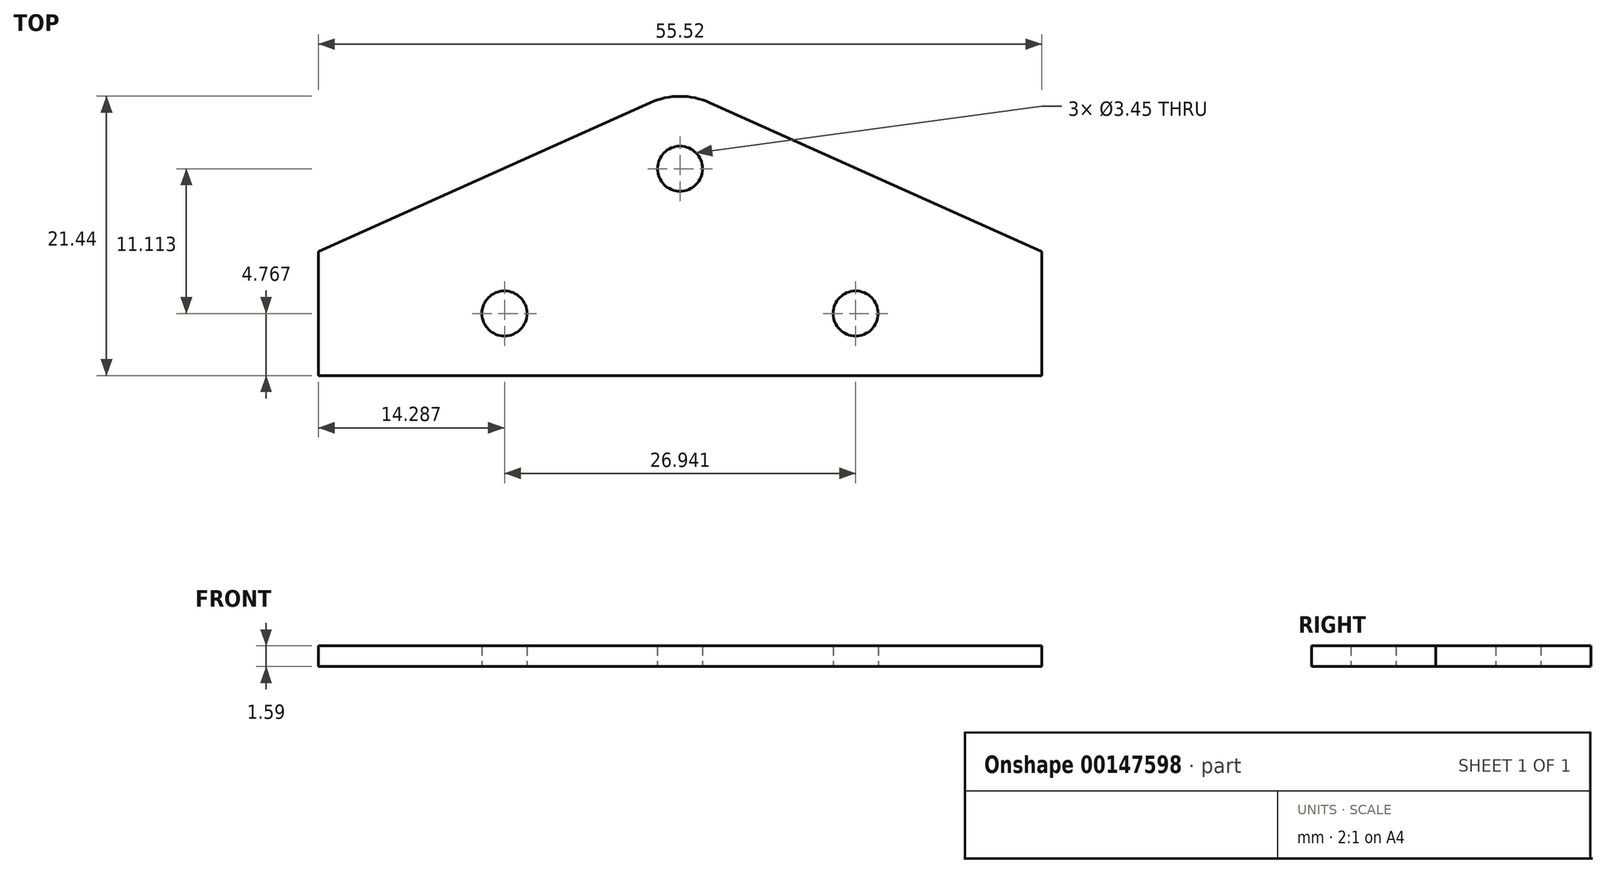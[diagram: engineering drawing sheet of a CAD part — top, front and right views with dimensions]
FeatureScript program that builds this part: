
annotation { "Feature Type Name" : "Feature", "Feature Type Description" : "" }
export const myFeature = defineFeature(function(context is Context, id is Id, definition is map)
    precondition{}
    {
        {
            var Q0;
            Q0=qCreatedBy(makeId("Top.planeOp"),FACE);
            var sketch = newSketch(context, id + "F0", { "sketchPlane" : qUnion([Q0])});
            skLineSegment(sketch, "E0.bottom", {"start": v(0, 0) * mm, "end": v(55.52, 0) * mm, "construction": true});
            skLineSegment(sketch, "E0.top", {"start": v(0, -9.53) * mm, "end": v(55.52, -9.53) * mm});
            skLineSegment(sketch, "E0.left", {"start": v(0, 0) * mm, "end": v(0, -9.53) * mm});
            skLineSegment(sketch, "E0.right", {"start": v(55.52, 0) * mm, "end": v(55.52, -9.52) * mm});
            skLineSegment(sketch, "E1", {"start": v(0, -4.76) * mm, "end": v(14.29, -4.76) * mm, "construction": true});
            skLineSegment(sketch, "E2", {"start": v(55.52, -4.76) * mm, "end": v(41.23, -4.76) * mm, "construction": true});
            skLineSegment(sketch, "E3", {"start": v(27.76, 0) * mm, "end": v(27.76, 6.35) * mm, "construction": true});
            skArc(sketch, "E4", {"start": v(30.03, 11.42) * mm, "mid": v(27.76, 11.9) * mm, "end": v(25.49, 11.42) * mm});
            skLineSegment(sketch, "E5", {"start": v(0, 0) * mm, "end": v(25.49, 11.42) * mm});
            skLineSegment(sketch, "E6", {"start": v(30.03, 11.42) * mm, "end": v(55.52, 0) * mm});
            skCircle(sketch, "E7", {"center": v(14.29, -4.76) * mm, "radius": 1.73 * mm});
            skCircle(sketch, "E8", {"center": v(41.23, -4.76) * mm, "radius": 1.73 * mm});
            skCircle(sketch, "E9", {"center": v(27.76, 6.35) * mm, "radius": 1.73 * mm});
            skSolve(sketch);
        }
        {
            var Q0;
            Q0=qSketchRegion(id+"F0",true);
            extrude(context, id + "F1", {"entities" : qUnion([Q0]), "depth" : 1.59 * mm});
        }
    });
